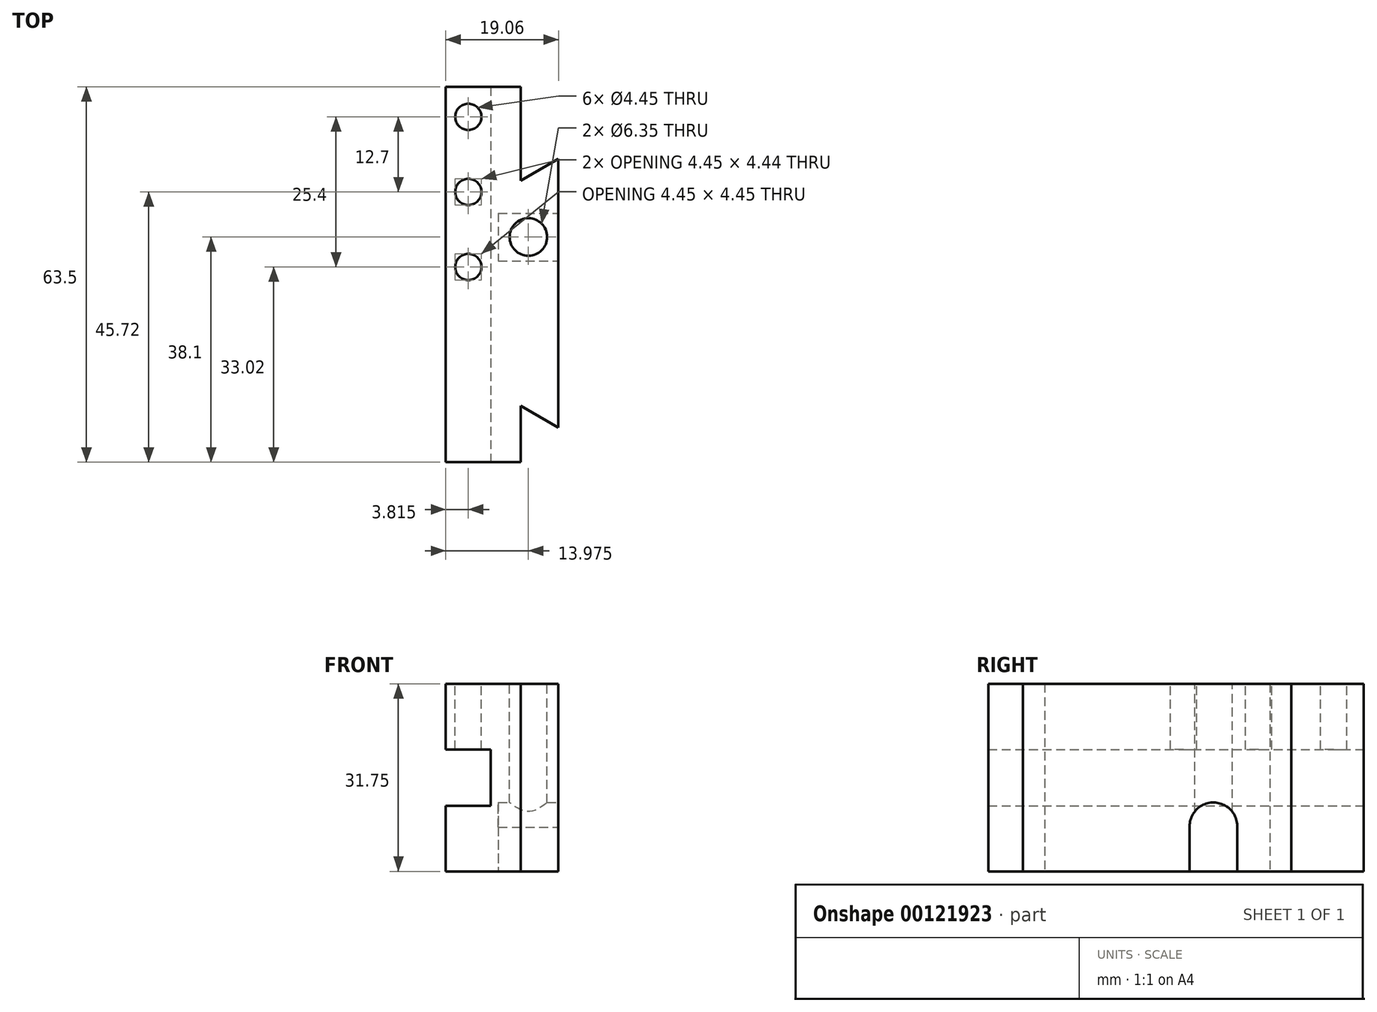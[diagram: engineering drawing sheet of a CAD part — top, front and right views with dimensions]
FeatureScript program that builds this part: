
annotation { "Feature Type Name" : "Feature", "Feature Type Description" : "" }
export const myFeature = defineFeature(function(context is Context, id is Id, definition is map)
    precondition{}
    {
        {
            var Q0;
            Q0=qCreatedBy(makeId("Top.planeOp"),FACE);
            var sketch = newSketch(context, id + "F0", { "sketchPlane" : qUnion([Q0])});
            skLineSegment(sketch, "E0.bottom", {"start": v(-9.53, 31.75) * mm, "end": v(3.18, 31.75) * mm});
            skLineSegment(sketch, "E0.top", {"start": v(-9.53, -31.75) * mm, "end": v(3.18, -31.75) * mm});
            skLineSegment(sketch, "E0.left", {"start": v(-9.53, 31.75) * mm, "end": v(-9.53, -31.75) * mm});
            skLineSegment(sketch, "E0.right", {"start": v(9.53, 19.54) * mm, "end": v(9.53, -25.9) * mm});
            skPoint(sketch, "E0.middle", {"position": v(0, 0) * mm});
            skLineSegment(sketch, "E1", {"start": v(3.18, 31.75) * mm, "end": v(3.18, -31.75) * mm});
            skLineSegment(sketch, "E2", {"start": v(3.18, -22.23) * mm, "end": v(9.52, -25.9) * mm});
            skLineSegment(sketch, "E3", {"start": v(3.18, 15.88) * mm, "end": v(9.53, 19.54) * mm});
            skPoint(sketch, "E4.orphan", {"position": v(9.53, 31.75) * mm});
            skPoint(sketch, "E5.orphan", {"position": v(9.53, -31.75) * mm});
            skSolve(sketch);
        }
        {
            var Q0;
            Q0 = qSketchRegion(id + "F0", true);
            var Q1;
            Q1=makeQuery(id+"F0.imprint","IMPRINT",FACE,{"disambiguationData":[TD([[makeQuery(id+"F0.imprint","IMPRINT",EDGE,{"derivedFrom":sQuery(id+"F0.wireOp",EDGE,"lLVAr5PG-q6IM-k4Fa-4QmQ-oKPcBxuEcoZY")}),1.0]])]});
            var Q2;
            Q2=makeQuery(id+"F0.imprint","IMPRINT",FACE,{"disambiguationData":[TD([[makeQuery(id+"F0.imprint","IMPRINT",EDGE,{"derivedFrom":sQuery(id+"F0.wireOp",EDGE,"e1L6cj2e-sHbK-xzKV-vFkU-KLUnSaXfdba3")}),1.0]])]});
            var Q3;
            Q3=makeQuery(id+"F0.imprint","IMPRINT",FACE,{"disambiguationData":[TD([[makeQuery(id+"F0.imprint","IMPRINT",EDGE,{"derivedFrom":sQuery(id+"F0.wireOp",EDGE,"PFCVr2ru-OPVT-Woux-SxbU-QPqUl11DG9NA")}),1.0]])]});
            var Q4;
            {var subQ0=sQuery(id+"F0.wireOp",EDGE,"Nmwffg0t-CmTc-h7Nb-HGEZ-nuW9bbGoD7yL");var subQ1=sQuery(id+"F0.wireOp",EDGE,"E1");var subQ2=makeQuery(id+"F0.imprint","INTERSECT",VERTEX,{"disambiguationData":[OD(0.0)],"derivedFrom":[subQ1,subQ0]});Q4=makeQuery(id+"F0.imprint","IMPRINT",FACE,{"disambiguationData":[TD([[makeQuery(id+"F0.imprint","IMPRINT",EDGE,{"disambiguationData":[TD([[subQ2,-1.0]])],"derivedFrom":subQ1}),1.0]])]});}
            var Q5;
            {var subQ0=sQuery(id+"F0.wireOp",EDGE,"Nmwffg0t-CmTc-h7Nb-HGEZ-nuW9bbGoD7yL");var subQ1=sQuery(id+"F0.wireOp",EDGE,"E1");var subQ2=makeQuery(id+"F0.imprint","INTERSECT",VERTEX,{"disambiguationData":[OD(0.0)],"derivedFrom":[subQ1,subQ0]});Q5=makeQuery(id+"F0.imprint","IMPRINT",FACE,{"disambiguationData":[TD([[makeQuery(id+"F0.imprint","IMPRINT",EDGE,{"disambiguationData":[TD([[subQ2,-1.0]])],"derivedFrom":subQ1}),-1.0]])]});}
            extrude(context, id + "F1", {"entities" : qUnion([Q0, Q1, Q2, Q3, Q4, Q5]), "depth" : 31.75 * mm});
        }
        {
            var Q0;
            Q0=makeQuery(id+"F1.opExtrude","SWEPT_FACE",FACE,{"disambiguationData":[OSD([sQuery(id+"F0.wireOp",EDGE,"E0.top")])]});
            var sketch = newSketch(context, id + "F2", { "sketchPlane" : qUnion([Q0])});
            skLineSegment(sketch, "E6.bottom", {"start": v(-17.15, 20.64) * mm, "end": v(-1.9, 20.64) * mm});
            skLineSegment(sketch, "E6.top", {"start": v(-17.15, 11.11) * mm, "end": v(-1.9, 11.11) * mm});
            skLineSegment(sketch, "E6.left", {"start": v(-17.15, 20.64) * mm, "end": v(-17.15, 11.11) * mm});
            skLineSegment(sketch, "E6.right", {"start": v(-1.9, 20.64) * mm, "end": v(-1.9, 11.11) * mm});
            skPoint(sketch, "E6.middle", {"position": v(-9.53, 15.88) * mm});
            skSolve(sketch);
        }
        {
            var Q0;
            Q0 = qSketchRegion(id + "F2", true);
            extrude(context, id + "F3", {"entities" : qUnion([Q0]), "operationType" : NewBodyOperationType.REMOVE, "endBound" : BoundingType.THROUGH_ALL, "oppositeDirection" : true, "depth" : 25.4 * mm});
        }
        {
            var Q0;
            Q0=makeQuery(id+"F1.opExtrude","CAP_FACE",FACE,{"disambiguationData":[OSD([sQuery(id+"F0.wireOp",EDGE,"E0.bottom"),sQuery(id+"F0.wireOp",EDGE,"E0.top"),sQuery(id+"F0.wireOp",EDGE,"E0.left"),sQuery(id+"F0.wireOp",EDGE,"E0.right"),sQuery(id+"F0.wireOp",EDGE,"E1"),sQuery(id+"F0.wireOp",EDGE,"E2"),sQuery(id+"F0.wireOp",EDGE,"E3")])],"isStart":false});
            var sketch = newSketch(context, id + "F4", { "sketchPlane" : qUnion([Q0])});
            skCircle(sketch, "E7", {"center": v(-5.72, 26.67) * mm, "radius": 2.22 * mm});
            skCircle(sketch, "E8", {"center": v(-5.72, 13.97) * mm, "radius": 2.22 * mm});
            skCircle(sketch, "E9", {"center": v(-5.72, 1.27) * mm, "radius": 2.22 * mm});
            skSolve(sketch);
        }
        {
            var Q0;
            Q0=makeQuery(id+"F4.imprint","IMPRINT",FACE,{"disambiguationData":[TD([[makeQuery(id+"F4.imprint","IMPRINT",EDGE,{"derivedFrom":sQuery(id+"F4.wireOp",EDGE,"E9")}),1.0]])]});
            var Q1;
            Q1=makeQuery(id+"F4.imprint","IMPRINT",FACE,{"disambiguationData":[TD([[makeQuery(id+"F4.imprint","IMPRINT",EDGE,{"derivedFrom":sQuery(id+"F4.wireOp",EDGE,"E8")}),1.0]])]});
            var Q2;
            Q2=makeQuery(id+"F4.imprint","IMPRINT",FACE,{"disambiguationData":[TD([[makeQuery(id+"F4.imprint","IMPRINT",EDGE,{"derivedFrom":sQuery(id+"F4.wireOp",EDGE,"E7")}),1.0]])]});
            extrude(context, id + "F5", {"entities" : qUnion([Q0, Q1, Q2]), "operationType" : NewBodyOperationType.REMOVE, "endBound" : BoundingType.UP_TO_NEXT, "oppositeDirection" : true, "depth" : 25.4 * mm});
        }
        {
            var Q0;
            Q0=makeQuery(id+"F1.opExtrude","CAP_FACE",FACE,{"disambiguationData":[OSD([sQuery(id+"F0.wireOp",EDGE,"E0.bottom"),sQuery(id+"F0.wireOp",EDGE,"E0.top"),sQuery(id+"F0.wireOp",EDGE,"E0.left"),sQuery(id+"F0.wireOp",EDGE,"E0.right"),sQuery(id+"F0.wireOp",EDGE,"E1"),sQuery(id+"F0.wireOp",EDGE,"E2"),sQuery(id+"F0.wireOp",EDGE,"E3")])],"isStart":false});
            var sketch = newSketch(context, id + "F6", { "sketchPlane" : qUnion([Q0])});
            skCircle(sketch, "E10", {"center": v(4.45, 6.35) * mm, "radius": 3.18 * mm});
            skSolve(sketch);
        }
        {
            var Q0;
            Q0 = qSketchRegion(id + "F6", true);
            extrude(context, id + "F7", {"entities" : qUnion([Q0]), "operationType" : NewBodyOperationType.REMOVE, "oppositeDirection" : true, "depth" : 25.4 * mm});
        }
        {
            var Q0;
            Q0=makeQuery(id+"F1.opExtrude","SWEPT_FACE",FACE,{"disambiguationData":[OSD([sQuery(id+"F0.wireOp",EDGE,"E0.right")])]});
            var sketch = newSketch(context, id + "F8", { "sketchPlane" : qUnion([Q0])});
            skArc(sketch, "E11", {"start": v(10.38, 7.45) * mm, "mid": v(6.43, 11.65) * mm, "end": v(2.32, 7.62) * mm});
            skLineSegment(sketch, "E12", {"start": v(10.38, 7.79) * mm, "end": v(10.38, 0) * mm});
            skLineSegment(sketch, "E13", {"start": v(2.32, 7.62) * mm, "end": v(2.32, 0) * mm});
            skLineSegment(sketch, "E14", {"start": v(10.38, 0) * mm, "end": v(2.32, 0) * mm});
            skSolve(sketch);
        }
        {
            var Q0;
            Q0 = qSketchRegion(id + "F8", true);
            extrude(context, id + "F9", {"entities" : qUnion([Q0]), "operationType" : NewBodyOperationType.REMOVE, "oppositeDirection" : true, "depth" : 10.16 * mm});
        }
    });
